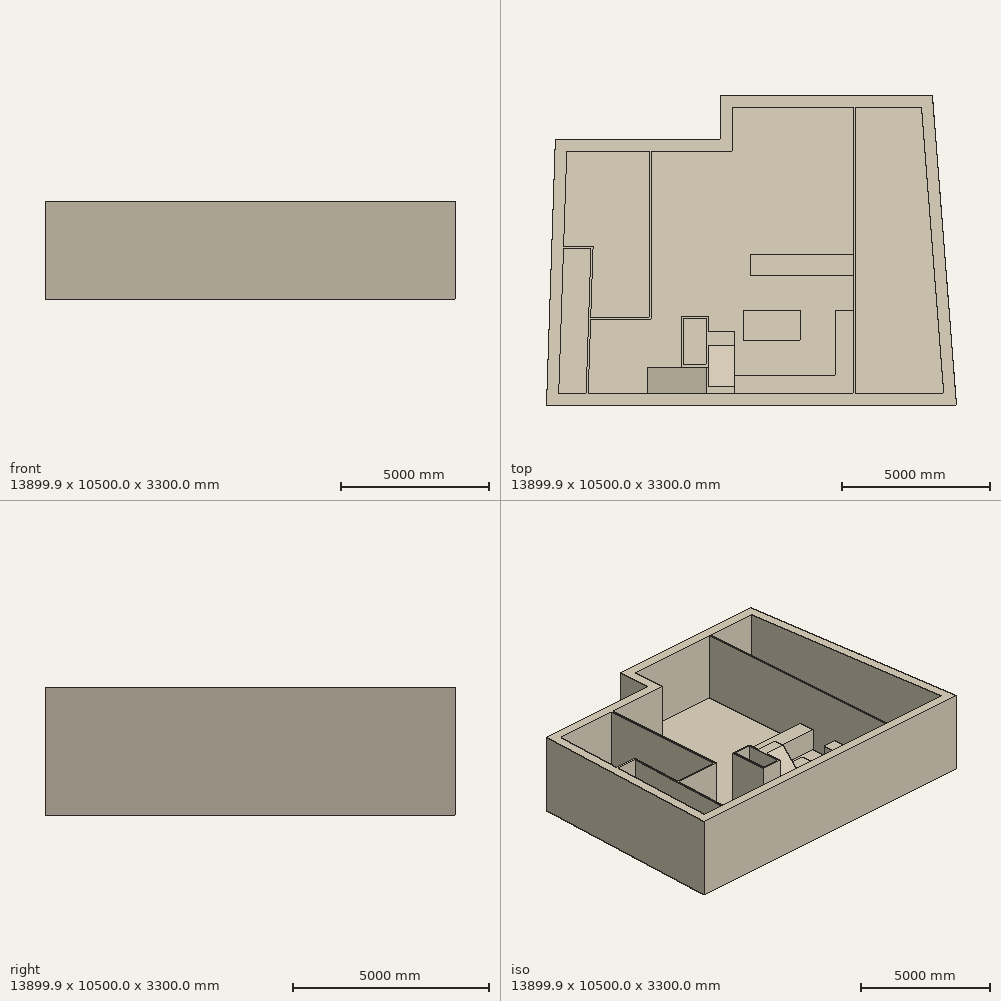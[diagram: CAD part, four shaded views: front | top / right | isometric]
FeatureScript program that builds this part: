
annotation { "Feature Type Name" : "Feature", "Feature Type Description" : "" }
export const myFeature = defineFeature(function(context is Context, id is Id, definition is map)
    precondition{}
    {
        {
            var Q0;
            Q0=qCreatedBy(makeId("Top.planeOp"),FACE);
            var sketch = newSketch(context, id + "F0", { "sketchPlane" : qUnion([Q0])});
            skLineSegment(sketch, "E0", {"start": v(0, 0) * mm, "end": v(14000, 0) * mm});
            skLineSegment(sketch, "E1", {"start": v(14000, 0) * mm, "end": v(12911.11, 14000) * mm});
            skLineSegment(sketch, "E2", {"start": v(12911.11, 14000) * mm, "end": v(12911.11, 29000) * mm});
            skLineSegment(sketch, "E3", {"start": v(12911.11, 29000) * mm, "end": v(800, 29000) * mm});
            skLineSegment(sketch, "E4", {"start": v(300, 14000) * mm, "end": v(800, 29000) * mm});
            skLineSegment(sketch, "E5", {"start": v(300, 14000) * mm, "end": v(300, 9000) * mm});
            skLineSegment(sketch, "E6", {"start": v(300, 9000) * mm, "end": v(0, 0) * mm});
            skLineSegment(sketch, "E7", {"start": v(14000, 0) * mm, "end": v(14000, 9000) * mm, "construction": true});
            skLineSegment(sketch, "E8", {"start": v(14000, 9000) * mm, "end": v(13300, 9000) * mm, "construction": true});
            skLineSegment(sketch, "E9", {"start": v(0, 0) * mm, "end": v(0, 9000) * mm, "construction": true});
            skLineSegment(sketch, "E10", {"start": v(0, 9000) * mm, "end": v(300, 9000) * mm, "construction": true});
            skLineSegment(sketch, "E11", {"start": v(100.06, 0) * mm, "end": v(400, 8998.33) * mm});
            skLineSegment(sketch, "E12", {"start": v(400, 8998.33) * mm, "end": v(400, 17000) * mm});
            skLineSegment(sketch, "E13", {"start": v(12204.04, 15353.33) * mm, "end": v(12581.52, 10500) * mm});
            skLineSegment(sketch, "E14", {"start": v(12581.52, 10500) * mm, "end": v(13183.33, 10500) * mm});
            skSolve(sketch);
        }
        {
            var Q0;
            Q0=qCreatedBy(makeId("Top.planeOp"),FACE);
            var sketch = newSketch(context, id + "F1", { "sketchPlane" : qUnion([Q0])});
            skLineSegment(sketch, "E15", {"start": v(100.06, 0) * mm, "end": v(400.06, 9000) * mm});
            skLineSegment(sketch, "E16", {"start": v(400.06, 9000) * mm, "end": v(6000, 9000) * mm});
            skLineSegment(sketch, "E17", {"start": v(6000, 9000) * mm, "end": v(6000, 10500) * mm});
            skLineSegment(sketch, "E18", {"start": v(6000, 10500) * mm, "end": v(13183.33, 10500) * mm});
            skLineSegment(sketch, "E19", {"start": v(13183.33, 10500) * mm, "end": v(14000, 0) * mm});
            skLineSegment(sketch, "E20", {"start": v(14000, 0) * mm, "end": v(100.06, 0) * mm});
            skLineSegment(sketch, "E21.0", {"start": v(6400, 8600) * mm, "end": v(6400, 10100) * mm});
            skLineSegment(sketch, "E21.1", {"start": v(12813.24, 10100) * mm, "end": v(13567.68, 400) * mm});
            skLineSegment(sketch, "E21.2", {"start": v(13567.68, 400) * mm, "end": v(513.61, 400) * mm});
            skLineSegment(sketch, "E21.3", {"start": v(6400, 10100) * mm, "end": v(12813.24, 10100) * mm});
            skLineSegment(sketch, "E21.4", {"start": v(513.61, 400) * mm, "end": v(786.94, 8600) * mm});
            skLineSegment(sketch, "E21.5", {"start": v(786.94, 8600) * mm, "end": v(6400, 8600) * mm});
            skSolve(sketch);
        }
        {
            var Q0;
            Q0 = qSketchRegion(id + "F1", true);
            extrude(context, id + "F2", {"entities" : qUnion([Q0]), "depth" : 2800 * mm, "offsetDistance" : 25 * mm});
        }
        {
            var Q0;
            Q0=qCreatedBy(makeId("Top.planeOp"),FACE);
            var sketch = newSketch(context, id + "F3", { "sketchPlane" : qUnion([Q0])});
            skLineSegment(sketch, "E22", {"start": v(100.06, 0) * mm, "end": v(14000, 0) * mm});
            skLineSegment(sketch, "E23", {"start": v(14000, 0) * mm, "end": v(13183.33, 10500) * mm});
            skLineSegment(sketch, "E24", {"start": v(13183.33, 10500) * mm, "end": v(6000, 10500) * mm});
            skLineSegment(sketch, "E25", {"start": v(6000, 10500) * mm, "end": v(6000, 9000) * mm});
            skLineSegment(sketch, "E26", {"start": v(6000, 9000) * mm, "end": v(400, 8998.33) * mm});
            skLineSegment(sketch, "E27", {"start": v(400, 8998.33) * mm, "end": v(100.06, 0) * mm});
            skSolve(sketch);
        }
        {
            var Q0;
            Q0 = qSketchRegion(id + "F3", true);
            extrude(context, id + "F4", {"entities" : qUnion([Q0]), "operationType" : NewBodyOperationType.ADD, "oppositeDirection" : true, "depth" : 500 * mm, "offsetDistance" : 25 * mm});
        }
        {
            var Q0;
            Q0=qCreatedBy(makeId("Top.planeOp"),FACE);
            var sketch = newSketch(context, id + "F5", { "sketchPlane" : qUnion([Q0])});
            skLineSegment(sketch, "E28", {"start": v(10570, 10100) * mm, "end": v(10570, 400) * mm});
            skLineSegment(sketch, "E29", {"start": v(10570, 400) * mm, "end": v(10500, 400) * mm});
            skLineSegment(sketch, "E30", {"start": v(10500, 400) * mm, "end": v(10500, 10100) * mm});
            skLineSegment(sketch, "E31", {"start": v(10500, 10100) * mm, "end": v(10570, 10100) * mm});
            skLineSegment(sketch, "E32", {"start": v(3670.06, 8600) * mm, "end": v(3670.06, 2900) * mm});
            skLineSegment(sketch, "E33", {"start": v(3670.06, 2900) * mm, "end": v(1597.5, 2900) * mm});
            skLineSegment(sketch, "E34.0", {"start": v(3600.06, 2970) * mm, "end": v(1599.83, 2970) * mm});
            skLineSegment(sketch, "E34.1", {"start": v(3600.06, 8600) * mm, "end": v(3600.06, 2970) * mm});
            skLineSegment(sketch, "E35", {"start": v(1680.83, 5400) * mm, "end": v(1599.83, 2970) * mm});
            skLineSegment(sketch, "E36.0", {"start": v(1608.46, 5330) * mm, "end": v(1444.13, 400) * mm});
            skLineSegment(sketch, "E37.trimOffspring", {"start": v(1597.5, 2900) * mm, "end": v(1514.17, 400) * mm});
            skLineSegment(sketch, "E38", {"start": v(3670.06, 8600) * mm, "end": v(3600.06, 8600) * mm});
            skLineSegment(sketch, "E39", {"start": v(1444.13, 400) * mm, "end": v(1514.17, 400) * mm});
            skLineSegment(sketch, "E40", {"start": v(1680.83, 5400) * mm, "end": v(680.28, 5400) * mm});
            skLineSegment(sketch, "E41", {"start": v(680.28, 5400) * mm, "end": v(677.94, 5330) * mm});
            skLineSegment(sketch, "E42", {"start": v(677.94, 5330) * mm, "end": v(1608.46, 5330) * mm});
            skLineSegment(sketch, "E43", {"start": v(5584.17, 400) * mm, "end": v(5584.17, 3000) * mm});
            skLineSegment(sketch, "E44", {"start": v(5584.17, 3000) * mm, "end": v(4670.06, 3000) * mm});
            skLineSegment(sketch, "E45", {"start": v(4670.06, 3000) * mm, "end": v(4670.06, 1300) * mm});
            skLineSegment(sketch, "E46", {"start": v(4670.06, 1300) * mm, "end": v(5514.17, 1300) * mm});
            skLineSegment(sketch, "E47.0", {"start": v(4740.06, 1370) * mm, "end": v(5514.17, 1370) * mm});
            skLineSegment(sketch, "E47.1", {"start": v(4740.06, 2930) * mm, "end": v(4740.06, 1370) * mm});
            skLineSegment(sketch, "E47.2", {"start": v(5514.17, 2930) * mm, "end": v(4740.06, 2930) * mm});
            skLineSegment(sketch, "E47.3", {"start": v(5514.17, 400) * mm, "end": v(5514.17, 1300) * mm});
            skLineSegment(sketch, "E48.trimOffspring", {"start": v(5514.17, 1370) * mm, "end": v(5514.17, 2930) * mm});
            skLineSegment(sketch, "E49", {"start": v(5514.17, 400) * mm, "end": v(5584.17, 400) * mm});
            skSolve(sketch);
        }
        {
            var Q0;
            Q0 = qSketchRegion(id + "F5", true);
            var Q1;
            Q1=sQuery(id+"F5.wireOp",EDGE,"E28");
            var Q2;
            Q2=makeQuery(id+"F2.opExtrude","CAP_FACE",FACE,{"disambiguationData":[OSD([sQuery(id+"F1.wireOp",EDGE,"E15"),sQuery(id+"F1.wireOp",EDGE,"E16"),sQuery(id+"F1.wireOp",EDGE,"E17"),sQuery(id+"F1.wireOp",EDGE,"E18"),sQuery(id+"F1.wireOp",EDGE,"E19"),sQuery(id+"F1.wireOp",EDGE,"E20"),sQuery(id+"F1.wireOp",EDGE,"E21.0"),sQuery(id+"F1.wireOp",EDGE,"E21.1"),sQuery(id+"F1.wireOp",EDGE,"E21.2"),sQuery(id+"F1.wireOp",EDGE,"E21.3"),sQuery(id+"F1.wireOp",EDGE,"E21.4"),sQuery(id+"F1.wireOp",EDGE,"E21.5")])],"isStart":false});
            extrude(context, id + "F6", {"entities" : qUnion([Q0]), "operationType" : NewBodyOperationType.ADD, "surfaceEntities" : qUnion([Q1]), "endBound" : BoundingType.UP_TO_SURFACE, "depth" : 3080 * mm, "endBoundEntityFace" : qUnion([Q2]), "offsetDistance" : 25 * mm});
        }
        {
            var Q0;
            Q0=makeQuery(id+"F6.boolean.opBoolean","SPLIT",FACE,{"disambiguationData":[TD([makeQuery(id+"F2.opExtrude","SWEPT_FACE",FACE,{"disambiguationData":[OSD([sQuery(id+"F1.wireOp",EDGE,"E21.0")])]})])],"derivedFrom":makeQuery(id+"F4.opExtrude","CAP_FACE",FACE,{"disambiguationData":[OSD([sQuery(id+"F3.wireOp",EDGE,"E22"),sQuery(id+"F3.wireOp",EDGE,"E23"),sQuery(id+"F3.wireOp",EDGE,"E24"),sQuery(id+"F3.wireOp",EDGE,"E25"),sQuery(id+"F3.wireOp",EDGE,"E26"),sQuery(id+"F3.wireOp",EDGE,"E27")])],"isStart":true})});
            var sketch = newSketch(context, id + "F7", { "sketchPlane" : qUnion([Q0])});
            skLineSegment(sketch, "E50", {"start": v(10500, 3200) * mm, "end": v(10500, 400) * mm});
            skLineSegment(sketch, "E51", {"start": v(10500, 400) * mm, "end": v(5584.17, 400) * mm});
            skLineSegment(sketch, "E52", {"start": v(5584.17, 400) * mm, "end": v(5584.17, 1000) * mm});
            skLineSegment(sketch, "E53", {"start": v(5584.17, 1000) * mm, "end": v(9900, 1000) * mm});
            skLineSegment(sketch, "E54", {"start": v(9900, 1000) * mm, "end": v(9900, 3200) * mm});
            skLineSegment(sketch, "E55", {"start": v(9900, 3200) * mm, "end": v(10500, 3200) * mm});
            skLineSegment(sketch, "E56.bottom", {"start": v(8700, 3200) * mm, "end": v(6784.17, 3200) * mm});
            skLineSegment(sketch, "E56.top", {"start": v(8700, 2200) * mm, "end": v(6784.17, 2200) * mm});
            skLineSegment(sketch, "E56.left", {"start": v(8700, 3200) * mm, "end": v(8700, 2200) * mm});
            skLineSegment(sketch, "E56.right", {"start": v(6784.17, 3200) * mm, "end": v(6784.17, 2200) * mm});
            skLineSegment(sketch, "E57.bottom", {"start": v(10500, 5100) * mm, "end": v(7000, 5100) * mm});
            skLineSegment(sketch, "E57.top", {"start": v(10500, 4400) * mm, "end": v(7000, 4400) * mm});
            skLineSegment(sketch, "E57.left", {"start": v(10500, 5100) * mm, "end": v(10500, 4400) * mm});
            skLineSegment(sketch, "E57.right", {"start": v(7000, 5100) * mm, "end": v(7000, 4400) * mm});
            skSolve(sketch);
        }
        {
            var Q0;
            Q0 = qSketchRegion(id + "F7", true);
            extrude(context, id + "F8", {"entities" : qUnion([Q0]), "operationType" : NewBodyOperationType.ADD, "depth" : 900 * mm, "offsetDistance" : 25 * mm});
        }
        {
            var Q0;
            {var subQ3=sQuery(id+"F1.wireOp",EDGE,"E21.2");Q0=makeQuery(id+"F6.boolean.opBoolean","SPLIT",FACE,{"disambiguationData":[TD([makeQuery(id+"F6.opExtrude","SWEPT_FACE",FACE,{"disambiguationData":[OSD([sQuery(id+"F5.wireOp",EDGE,"E37.trimOffspring")])]})])],"derivedFrom":makeQuery(id+"F2.opExtrude","SWEPT_FACE",FACE,{"disambiguationData":[OSD([subQ3])]})});}
            var sketch = newSketch(context, id + "F9", { "sketchPlane" : qUnion([Q0])});
            skLineSegment(sketch, "E58", {"start": v(-5584.17, 1051.03) * mm, "end": v(-3815.35, 0) * mm});
            skLineSegment(sketch, "E59", {"start": v(-3815.35, 0) * mm, "end": v(-3514.17, 0) * mm});
            skLineSegment(sketch, "E60", {"start": v(-3514.17, 170) * mm, "end": v(-5584.17, 1400) * mm});
            skLineSegment(sketch, "E61", {"start": v(-5584.17, 1400) * mm, "end": v(-5584.17, 1051.03) * mm});
            skLineSegment(sketch, "E62", {"start": v(-3514.17, 0) * mm, "end": v(-3514.17, 170) * mm});
            skSolve(sketch);
        }
        {
            var Q0;
            Q0 = qSketchRegion(id + "F9", true);
            extrude(context, id + "F10", {"entities" : qUnion([Q0]), "operationType" : NewBodyOperationType.ADD, "depth" : 900 * mm, "offsetDistance" : 25 * mm});
        }
        {
            var Q0;
            Q0=makeQuery(id+"F6.opExtrude","SWEPT_FACE",FACE,{"disambiguationData":[OSD([sQuery(id+"F5.wireOp",EDGE,"E43")])]});
            var sketch = newSketch(context, id + "F11", { "sketchPlane" : qUnion([Q0])});
            skLineSegment(sketch, "E63", {"start": v(630.45, 1358.4) * mm, "end": v(2042.12, 2800) * mm});
            skLineSegment(sketch, "E64", {"start": v(2042.12, 2800) * mm, "end": v(2500, 2800) * mm});
            skLineSegment(sketch, "E65", {"start": v(2500, 2800) * mm, "end": v(639.44, 900) * mm});
            skLineSegment(sketch, "E66", {"start": v(639.44, 900) * mm, "end": v(400, 900) * mm});
            skLineSegment(sketch, "E67", {"start": v(400, 900) * mm, "end": v(400, 1358.4) * mm});
            skLineSegment(sketch, "E68", {"start": v(400, 1358.4) * mm, "end": v(630.45, 1358.4) * mm});
            skSolve(sketch);
        }
        {
            var Q0;
            Q0 = qSketchRegion(id + "F11", true);
            extrude(context, id + "F12", {"entities" : qUnion([Q0]), "operationType" : NewBodyOperationType.ADD, "depth" : 900 * mm, "offsetDistance" : 25 * mm});
        }
        {
            var Q0;
            {var subQ3=sQuery(id+"F1.wireOp",EDGE,"E21.2");Q0=makeQuery(id+"F12.boolean.opBoolean","SPLIT",FACE,{"disambiguationData":[TD([makeQuery(id+"F2.opExtrude","SWEPT_FACE",FACE,{"disambiguationData":[OSD([subQ3])]})])],"derivedFrom":makeQuery(id+"F6.opExtrude","SWEPT_FACE",FACE,{"disambiguationData":[OSD([sQuery(id+"F5.wireOp",EDGE,"E43")])]})});}
            var sketch = newSketch(context, id + "F13", { "sketchPlane" : qUnion([Q0])});
            skLineSegment(sketch, "E69.0.0", {"start": v(1300, 2800) * mm, "end": v(1300, 1358.4) * mm});
            skLineSegment(sketch, "E69.0.1", {"start": v(1300, 1358.4) * mm, "end": v(400, 1358.4) * mm});
            skLineSegment(sketch, "E69.0.2", {"start": v(400, 1358.4) * mm, "end": v(400, 2800) * mm});
            skLineSegment(sketch, "E69.0.3", {"start": v(400, 2800) * mm, "end": v(1300, 2800) * mm});
            skSolve(sketch);
        }
        {
            var Q0;
            Q0 = qSketchRegion(id + "F13", true);
            var Q1;
            {var subQ3=sQuery(id+"F1.wireOp",EDGE,"E21.2");Q1=makeQuery(id+"F12.boolean.opBoolean","SPLIT",FACE,{"disambiguationData":[TD([makeQuery(id+"F2.opExtrude","SWEPT_FACE",FACE,{"disambiguationData":[OSD([subQ3])]})])],"derivedFrom":makeQuery(id+"F6.opExtrude","SWEPT_FACE",FACE,{"disambiguationData":[OSD([sQuery(id+"F5.wireOp",EDGE,"E43")])]})});}
            extrude(context, id + "F14", {"entities" : qUnion([Q0]), "operationType" : NewBodyOperationType.REMOVE, "oppositeDirection" : true, "depth" : 190 * mm, "endBoundEntityFace" : qUnion([Q1]), "offsetDistance" : 25 * mm});
        }
    });
